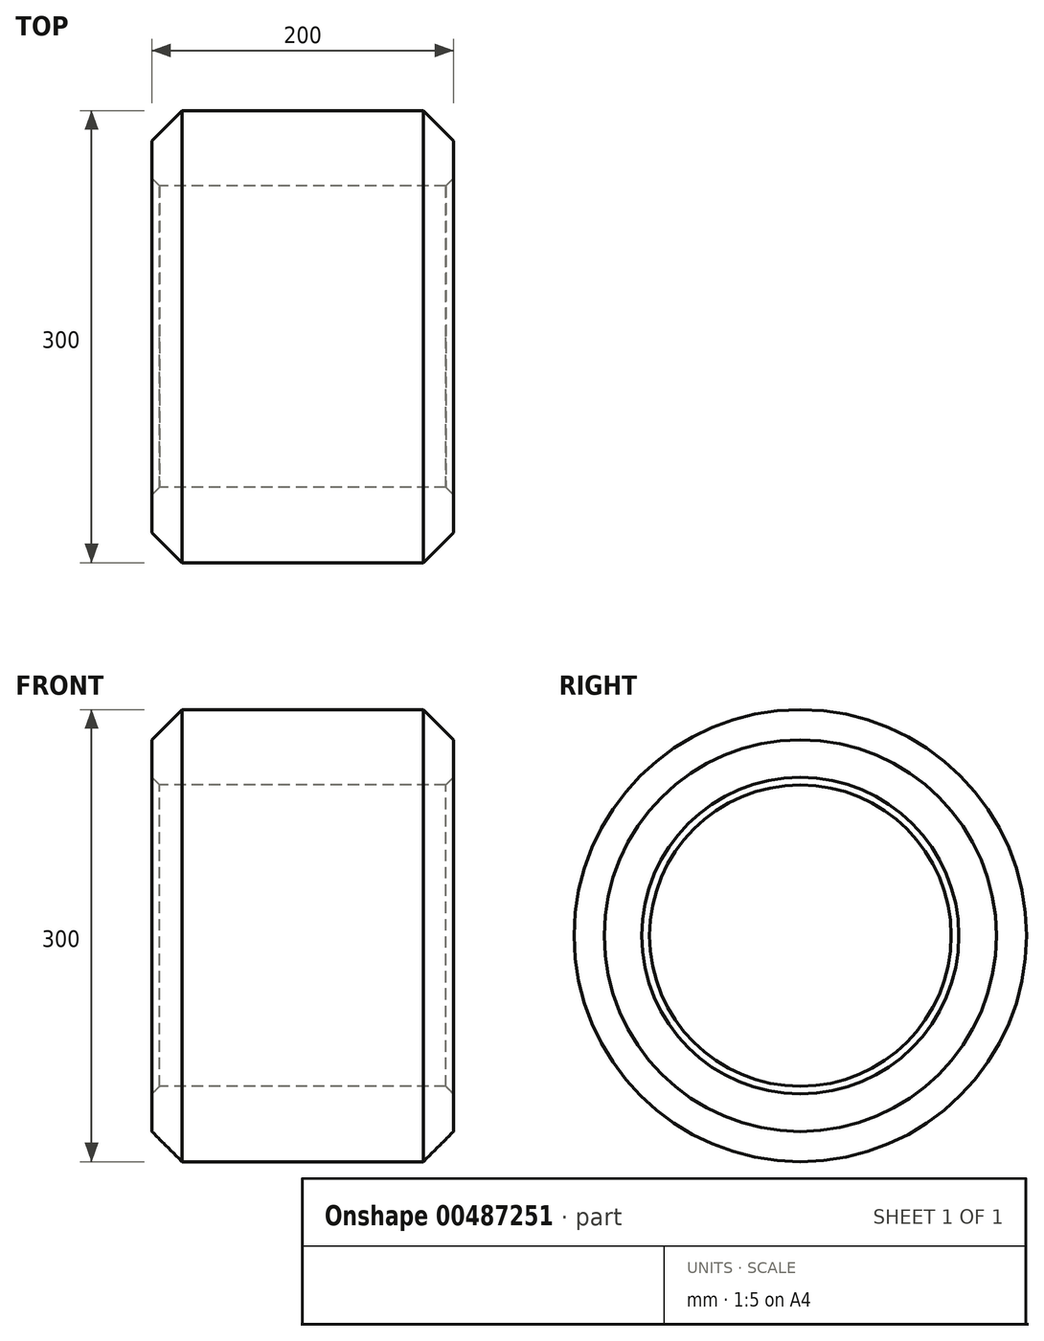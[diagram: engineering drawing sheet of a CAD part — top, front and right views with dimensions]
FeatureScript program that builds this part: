
annotation { "Feature Type Name" : "Feature", "Feature Type Description" : "" }
export const myFeature = defineFeature(function(context is Context, id is Id, definition is map)
    precondition{}
    {
        {
            var Q0;
            Q0=qCreatedBy(makeId("Right.planeOp"),FACE);
            var sketch = newSketch(context, id + "F0", { "sketchPlane" : qUnion([Q0])});
            skCircle(sketch, "E0", {"center": v(0, 0) * mm, "radius": 150 * mm});
            skCircle(sketch, "E1", {"center": v(0, 0) * mm, "radius": 100 * mm});
            skSolve(sketch);
        }
        {
            var Q0;
            Q0=makeQuery(id+"F0.imprint","IMPRINT",FACE,{"disambiguationData":[TD([[makeQuery(id+"F0.imprint","IMPRINT",EDGE,{"derivedFrom":sQuery(id+"F0.wireOp",EDGE,"E0")}),1.0]])]});
            extrude(context, id + "F1", {"entities" : qUnion([Q0]), "depth" : 200 * mm});
        }
        {
            var Q0;
            Q0=makeQuery(id+"F1.opExtrude","CAP_EDGE",EDGE,{"disambiguationData":[OSD([sQuery(id+"F0.wireOp",EDGE,"E0")])],"isStart":false});
            chamfer(context, id + "F2", {"entities" : qUnion([Q0]), "width" : 20 * mm, "tangentPropagation" : true});
        }
        {
            var Q0;
            Q0=makeQuery(id+"F1.opExtrude","CAP_EDGE",EDGE,{"disambiguationData":[OSD([sQuery(id+"F0.wireOp",EDGE,"E0")])],"isStart":true});
            chamfer(context, id + "F3", {"entities" : qUnion([Q0]), "width" : 20 * mm, "tangentPropagation" : true});
        }
        {
            var Q0;
            Q0=makeQuery(id+"F1.opExtrude","CAP_EDGE",EDGE,{"disambiguationData":[OSD([sQuery(id+"F0.wireOp",EDGE,"E1")])],"isStart":false});
            chamfer(context, id + "F4", {"entities" : qUnion([Q0]), "width" : 5.08 * mm, "tangentPropagation" : true});
        }
        {
            var Q0;
            Q0=makeQuery(id+"F1.opExtrude","CAP_EDGE",EDGE,{"disambiguationData":[OSD([sQuery(id+"F0.wireOp",EDGE,"E1")])],"isStart":true});
            chamfer(context, id + "F5", {"entities" : qUnion([Q0]), "width" : 5.08 * mm, "tangentPropagation" : true});
        }
    });
